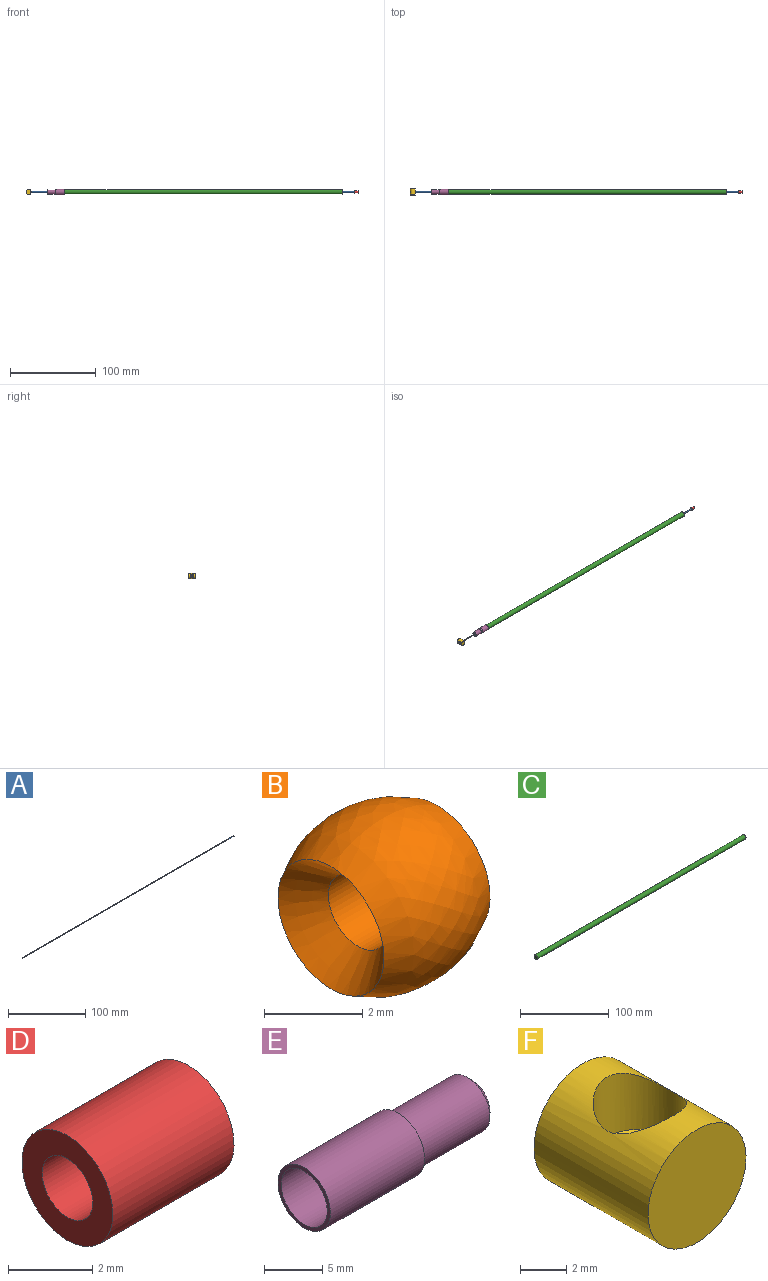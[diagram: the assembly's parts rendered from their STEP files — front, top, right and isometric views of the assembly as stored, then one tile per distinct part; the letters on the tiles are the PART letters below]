
ASSEMBLY  parts=6 mates=6
PART A: 3 faces, bbox 386x1.2x1.2 mm
  f0: plane 1.22x1.22mm, normal (-1,0,0), area 1.2mm2, adj f2
  f1: plane 1.22x1.22mm, normal (1,0,0), area 1.2mm2, adj f2
  f2: cylinder r=0.61mm len=386.03mm, axis (-1,0,0), area 1478.6mm2, adj f0,f1
PART B: 4 faces, bbox 3x4x4 mm
  f0: plane 3.05x3.05mm, normal (1,0,0), area 5mm2, adj f1,f2
  f1: revolved ~3.96x3.96mm, area 37.1mm2, adj f0,f3
  f2: cylinder r=0.85mm len=2.27mm, axis (-1,0,0), area 12.2mm2, adj f0,f3
  f3: cone r=0.85mm half-angle=41deg, axis (-1,0,0), area 7.7mm2, adj f1,f2
PART C: 3 faces, bbox 331.8x5.5x5.5 mm
  f0: plane 5.54x5.54mm, normal (-1,0,0), area 24.1mm2, adj f2
  f1: plane 5.54x5.54mm, normal (1,0,0), area 24.1mm2, adj f2
  f2: cylinder r=2.77mm len=331.77mm, axis (-1,0,0), area 5771.4mm2, adj f0,f1
PART D: 4 faces, bbox 4.1x3x3 mm
  f0: plane 3.05x3.05mm, normal (-1,0,0), area 5mm2, adj f2,f3
  f1: plane 3.05x3.05mm, normal (1,0,0), area 5mm2, adj f2,f3
  f2: cylinder r=1.52mm len=4.06mm, axis (-1,0,0), area 38.9mm2, adj f0,f1
  f3: cylinder r=0.85mm len=4.06mm, axis (-1,0,0), area 21.7mm2, adj f0,f1
PART E: 9 faces, bbox 20.3x6.4x6.4 mm
  f0: cone r=0mm half-angle=59deg, axis (-1,0,0), area 24.3mm2, adj f7,f8
  f1: plane 6.35x6.35mm, normal (-1,0,0), area 7.1mm2, adj f5,f7
  f2: plane 4.45x4.45mm, normal (1,0,0), area 11.9mm2, adj f6,f8
  f3: cylinder r=2.73mm len=8.38mm, axis (-1,0,0), area 143.8mm2, adj f4,f6
  f4: plane 6.35x6.35mm, normal (1,0,0), area 8.2mm2, adj f3,f5
  f5: cylinder r=3.17mm len=11.43mm, axis (-1,0,0), area 228mm2, adj f1,f4
  f6: cone r=2.73mm half-angle=45deg, axis (-1,0,0), area 11.2mm2, adj f2,f3
  f7: cylinder r=2.79mm len=9.19mm, axis (-1,0,0), area 161.4mm2, adj f0,f1
  f8: cylinder r=1.08mm len=10.1mm, axis (1,0,0), area 68.5mm2, adj f0,f2
PART F: 6 faces, bbox 6x7x6 mm
  f0: cone r=0mm half-angle=59deg, axis (0,0,1), area 11.8mm2, adj f3,f4
  f1: plane 5.99x5.99mm, normal (0,-1,0), area 28.2mm2, adj f5
  f2: plane 5.99x5.99mm, normal (0,1,0), area 28.2mm2, adj f5
  f3: cylinder r=2.03mm len=4.06mm, axis (0,0,1), area 35.7mm2, adj f0,f5
  f4: cylinder r=0.95mm len=2.17mm, axis (0,0,-1), area 12.5mm2, adj f0,f5
  f5: cylinder r=3mm len=6.99mm, axis (0,-1,0), area 114.8mm2, adj f1,f2,f3,f4
PLACE A t=(-78.7,41.15,-32.16)mm
PLACE B t=(-78.7,41.15,-32.16)mm
PLACE C t=(-42.82,41.15,-32.16)mm
PLACE D t=(303.26,41.15,-32.16)mm
PLACE E rot(axis=(0,1,0),180deg) t=(-33.63,41.15,-32.16)mm
PLACE F rot(axis=(0.71,0,-0.71),180deg) t=(-72.84,37.66,-29.16)mm
MATE cylindrical E.f0 <-> C.f2  axis (1,0,0) through (-42.82,41.15,-32.16)mm
MATE cylindrical B.f2 <-> A.f2  axis (-1,0,0) through (-78.7,41.15,-32.16)mm
MATE cylindrical F.f0 <-> B.f2  axis (-1,0,0) through (-75.66,41.15,-32.16)mm
MATE cylindrical A.f2 <-> C.f2  axis (-1,0,0) through (-78.7,41.15,-32.16)mm
MATE cylindrical D.f2 <-> A.f2  axis (1,0,0) through (307.33,41.15,-32.16)mm
MATE cylindrical D.f2 <-> A.f2  axis (1,0,0) through (307.33,41.15,-32.16)mm
